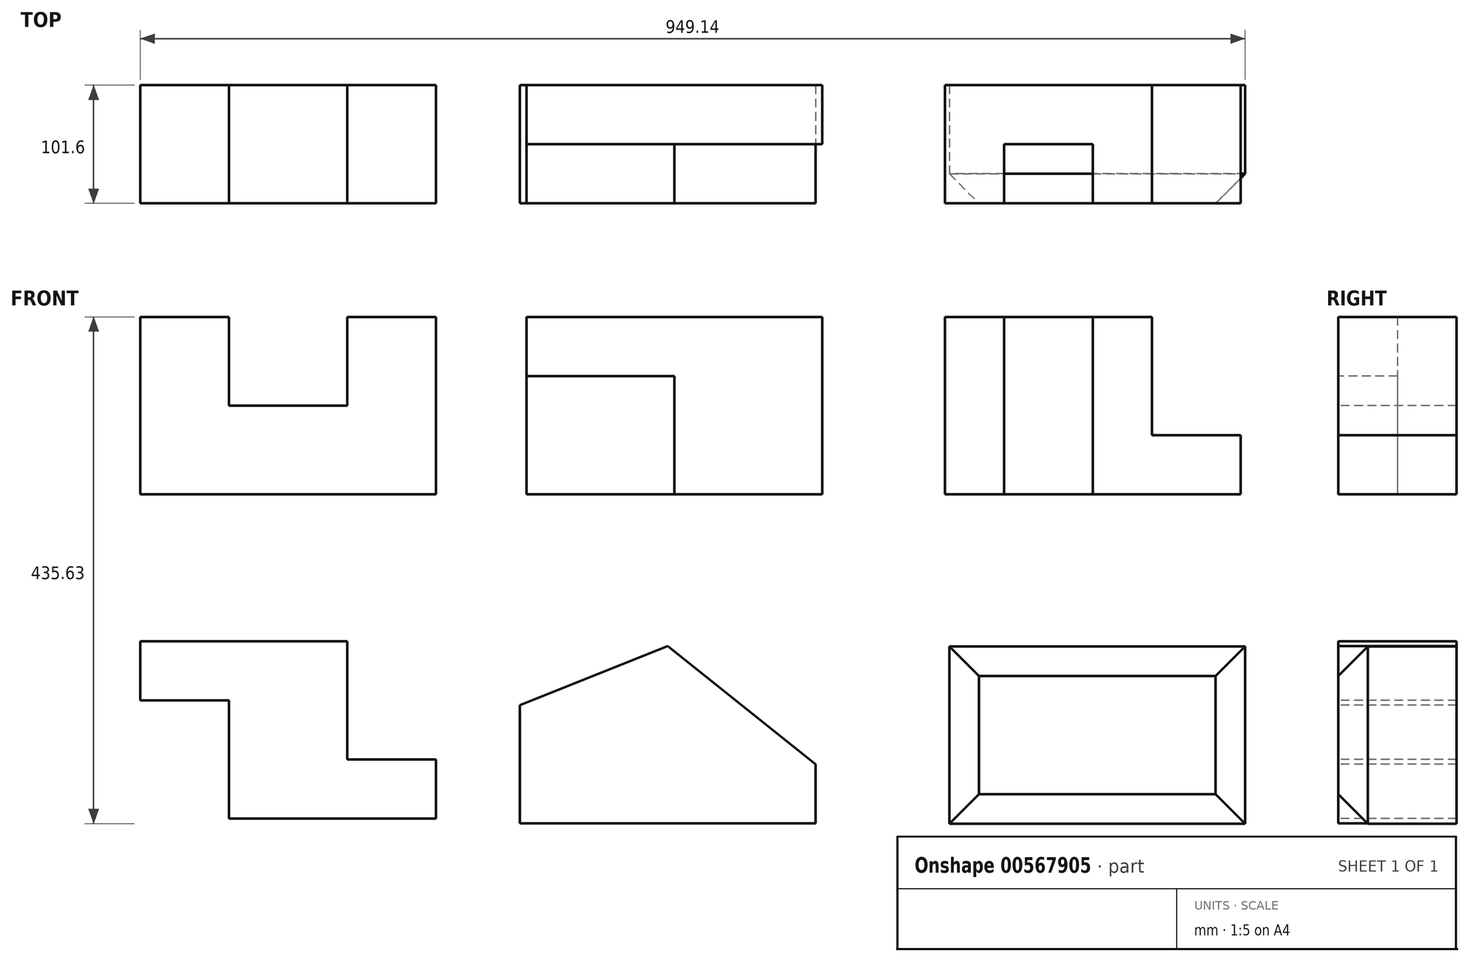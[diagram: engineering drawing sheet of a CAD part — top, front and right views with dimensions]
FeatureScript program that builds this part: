
annotation { "Feature Type Name" : "Feature", "Feature Type Description" : "" }
export const myFeature = defineFeature(function(context is Context, id is Id, definition is map)
    precondition{}
    {
        {
            var Q0;
            Q0=qCreatedBy(makeId("Front.planeOp"),FACE);
            var sketch = newSketch(context, id + "F0", { "sketchPlane" : qUnion([Q0])});
            skLineSegment(sketch, "E0", {"start": v(0, 0) * mm, "end": v(254, 0) * mm});
            skLineSegment(sketch, "E1", {"start": v(0, 152.4) * mm, "end": v(76.2, 152.4) * mm});
            skLineSegment(sketch, "E2", {"start": v(76.2, 152.4) * mm, "end": v(76.2, 76.2) * mm});
            skLineSegment(sketch, "E3", {"start": v(76.2, 76.2) * mm, "end": v(177.8, 76.2) * mm});
            skLineSegment(sketch, "E4", {"start": v(177.8, 76.2) * mm, "end": v(177.8, 152.4) * mm});
            skLineSegment(sketch, "E5", {"start": v(177.8, 152.4) * mm, "end": v(254, 152.4) * mm});
            skLineSegment(sketch, "E6", {"start": v(254, 152.4) * mm, "end": v(254, 0) * mm});
            skLineSegment(sketch, "E7", {"start": v(0, 0) * mm, "end": v(0, 152.4) * mm});
            skSolve(sketch);
        }
        {
            var Q0;
            Q0=makeQuery(id+"F0.imprint","IMPRINT",FACE,{"disambiguationData":[TD([[makeQuery(id+"F0.imprint","IMPRINT",EDGE,{"derivedFrom":sQuery(id+"F0.wireOp",EDGE,"E0")}),1.0]])]});
            extrude(context, id + "F1", {"entities" : qUnion([Q0]), "oppositeDirection" : true, "depth" : 101.6 * mm, "offsetDistance" : 25.4 * mm});
        }
        {
            var Q0;
            Q0=qCreatedBy(makeId("Top.planeOp"),FACE);
            var sketch = newSketch(context, id + "F2", { "sketchPlane" : qUnion([Q0])});
            skLineSegment(sketch, "E8", {"start": v(331.96, 0) * mm, "end": v(331.96, 101.6) * mm});
            skLineSegment(sketch, "E9", {"start": v(331.96, 101.6) * mm, "end": v(585.96, 101.6) * mm});
            skLineSegment(sketch, "E10", {"start": v(585.96, 101.6) * mm, "end": v(585.96, 50.8) * mm});
            skLineSegment(sketch, "E11", {"start": v(585.96, 50.8) * mm, "end": v(458.96, 50.8) * mm});
            skLineSegment(sketch, "E12", {"start": v(458.96, 50.8) * mm, "end": v(458.96, 0) * mm});
            skLineSegment(sketch, "E13", {"start": v(458.96, 0) * mm, "end": v(331.96, 0) * mm});
            skSolve(sketch);
        }
        {
            var Q0;
            Q0=makeQuery(id+"F2.imprint","IMPRINT",FACE,{"disambiguationData":[TD([[makeQuery(id+"F2.imprint","IMPRINT",EDGE,{"derivedFrom":sQuery(id+"F2.wireOp",EDGE,"E8")}),-1.0]])]});
            extrude(context, id + "F3", {"entities" : qUnion([Q0]), "depth" : 152.4 * mm, "offsetDistance" : 25.4 * mm});
        }
        {
            var Q0;
            Q0=qCreatedBy(makeId("Top.planeOp"),FACE);
            var sketch = newSketch(context, id + "F4", { "sketchPlane" : qUnion([Q0])});
            skLineSegment(sketch, "E14", {"start": v(691.2, 0) * mm, "end": v(691.2, 101.6) * mm});
            skLineSegment(sketch, "E15", {"start": v(691.2, 101.6) * mm, "end": v(945.2, 101.6) * mm});
            skLineSegment(sketch, "E16", {"start": v(945.2, 101.6) * mm, "end": v(945.2, 0) * mm});
            skLineSegment(sketch, "E17", {"start": v(691.2, 0) * mm, "end": v(742, 0) * mm});
            skLineSegment(sketch, "E18", {"start": v(742, 0) * mm, "end": v(742, 50.8) * mm});
            skLineSegment(sketch, "E19", {"start": v(742, 50.8) * mm, "end": v(818.2, 50.8) * mm});
            skLineSegment(sketch, "E20", {"start": v(818.2, 50.8) * mm, "end": v(818.2, 0) * mm});
            skLineSegment(sketch, "E21", {"start": v(818.2, 0) * mm, "end": v(945.2, 0) * mm});
            skSolve(sketch);
        }
        {
            var Q0;
            Q0=makeQuery(id+"F4.imprint","IMPRINT",FACE,{"disambiguationData":[TD([[makeQuery(id+"F4.imprint","IMPRINT",EDGE,{"derivedFrom":sQuery(id+"F4.wireOp",EDGE,"E14")}),-1.0]])]});
            extrude(context, id + "F5", {"entities" : qUnion([Q0]), "depth" : 152.4 * mm, "offsetDistance" : 25.4 * mm});
        }
        {
            var Q0;
            Q0=makeQuery(id+"F3.opExtrude","SWEPT_FACE",FACE,{"disambiguationData":[OSD([sQuery(id+"F2.wireOp",EDGE,"E13")])]});
            var sketch = newSketch(context, id + "F6", { "sketchPlane" : qUnion([Q0])});
            skLineSegment(sketch, "E22.bottom", {"start": v(331.96, 152.4) * mm, "end": v(458.96, 152.4) * mm});
            skLineSegment(sketch, "E22.top", {"start": v(331.96, 101.6) * mm, "end": v(458.96, 101.6) * mm});
            skLineSegment(sketch, "E22.left", {"start": v(331.96, 152.4) * mm, "end": v(331.96, 101.6) * mm});
            skLineSegment(sketch, "E22.right", {"start": v(458.96, 152.4) * mm, "end": v(458.96, 101.6) * mm});
            skSolve(sketch);
        }
        {
            var Q0;
            Q0=makeQuery(id+"F6.imprint","IMPRINT",FACE,{"disambiguationData":[TD([[makeQuery(id+"F6.imprint","IMPRINT",EDGE,{"derivedFrom":sQuery(id+"F6.wireOp",EDGE,"E22.bottom")}),1.0]])]});
            extrude(context, id + "F7", {"entities" : qUnion([Q0]), "operationType" : NewBodyOperationType.REMOVE, "oppositeDirection" : true, "depth" : 50.8 * mm, "offsetDistance" : 25.4 * mm});
        }
        {
            var Q0;
            Q0=makeQuery(id+"F5.opExtrude","SWEPT_FACE",FACE,{"disambiguationData":[OSD([sQuery(id+"F4.wireOp",EDGE,"E16")])]});
            var sketch = newSketch(context, id + "F8", { "sketchPlane" : qUnion([Q0])});
            skLineSegment(sketch, "E23.bottom", {"start": v(0, 152.4) * mm, "end": v(101.6, 152.4) * mm});
            skLineSegment(sketch, "E23.top", {"start": v(0, 50.8) * mm, "end": v(101.6, 50.8) * mm});
            skLineSegment(sketch, "E23.left", {"start": v(0, 152.4) * mm, "end": v(0, 50.8) * mm});
            skLineSegment(sketch, "E23.right", {"start": v(101.6, 152.4) * mm, "end": v(101.6, 50.8) * mm});
            skSolve(sketch);
        }
        {
            var Q0;
            Q0 = qSketchRegion(id + "F8", true);
            extrude(context, id + "F9", {"entities" : qUnion([Q0]), "operationType" : NewBodyOperationType.REMOVE, "oppositeDirection" : true, "depth" : 76.2 * mm, "offsetDistance" : 25.4 * mm});
        }
        {
            var Q0;
            Q0=qCreatedBy(makeId("Front.planeOp"),FACE);
            var sketch = newSketch(context, id + "F10", { "sketchPlane" : qUnion([Q0])});
            skLineSegment(sketch, "E24", {"start": v(0, -126.4) * mm, "end": v(254, -126.4) * mm});
            skLineSegment(sketch, "E25", {"start": v(254, -126.4) * mm, "end": v(254, -278.8) * mm});
            skLineSegment(sketch, "E26", {"start": v(254, -278.8) * mm, "end": v(0, -278.8) * mm});
            skLineSegment(sketch, "E27", {"start": v(0, -278.8) * mm, "end": v(0, -126.4) * mm});
            skSolve(sketch);
        }
        {
            var Q0;
            Q0=makeQuery(id+"F10.imprint","IMPRINT",FACE,{"disambiguationData":[TD([[makeQuery(id+"F10.imprint","IMPRINT",EDGE,{"derivedFrom":sQuery(id+"F10.wireOp",EDGE,"E24")}),-1.0]])]});
            extrude(context, id + "F11", {"entities" : qUnion([Q0]), "oppositeDirection" : true, "depth" : 101.6 * mm, "offsetDistance" : 25.4 * mm});
        }
        {
            var Q0;
            Q0=makeQuery(id+"F11.opExtrude","CAP_FACE",FACE,{"disambiguationData":[OSD([sQuery(id+"F10.wireOp",EDGE,"E24"),sQuery(id+"F10.wireOp",EDGE,"E25"),sQuery(id+"F10.wireOp",EDGE,"E26"),sQuery(id+"F10.wireOp",EDGE,"E27")])],"isStart":true});
            var sketch = newSketch(context, id + "F12", { "sketchPlane" : qUnion([Q0])});
            skLineSegment(sketch, "E28.bottom", {"start": v(0, -278.8) * mm, "end": v(76.2, -278.8) * mm});
            skLineSegment(sketch, "E28.top", {"start": v(0, -177.2) * mm, "end": v(76.2, -177.2) * mm});
            skLineSegment(sketch, "E28.left", {"start": v(0, -278.8) * mm, "end": v(0, -177.2) * mm});
            skLineSegment(sketch, "E28.right", {"start": v(76.2, -278.8) * mm, "end": v(76.2, -177.2) * mm});
            skLineSegment(sketch, "E29.bottom", {"start": v(254, -126.4) * mm, "end": v(177.8, -126.4) * mm});
            skLineSegment(sketch, "E29.top", {"start": v(254, -228) * mm, "end": v(177.8, -228) * mm});
            skLineSegment(sketch, "E29.left", {"start": v(254, -126.4) * mm, "end": v(254, -228) * mm});
            skLineSegment(sketch, "E29.right", {"start": v(177.8, -126.4) * mm, "end": v(177.8, -228) * mm});
            skSolve(sketch);
        }
        {
            var Q0;
            Q0=makeQuery(id+"F12.imprint","IMPRINT",FACE,{"disambiguationData":[TD([[makeQuery(id+"F12.imprint","IMPRINT",EDGE,{"derivedFrom":sQuery(id+"F12.wireOp",EDGE,"E28.bottom")}),-1.0]])]});
            var Q1;
            Q1=makeQuery(id+"F12.imprint","IMPRINT",FACE,{"disambiguationData":[TD([[makeQuery(id+"F12.imprint","IMPRINT",EDGE,{"derivedFrom":sQuery(id+"F12.wireOp",EDGE,"E29.bottom")}),-1.0]])]});
            extrude(context, id + "F13", {"entities" : qUnion([Q0, Q1]), "operationType" : NewBodyOperationType.REMOVE, "oppositeDirection" : true, "depth" : 101.6 * mm, "offsetDistance" : 25.4 * mm});
        }
        {
            var Q0;
            Q0=qCreatedBy(makeId("Front.planeOp"),FACE);
            var sketch = newSketch(context, id + "F14", { "sketchPlane" : qUnion([Q0])});
            skLineSegment(sketch, "E30", {"start": v(326.29, -130.56) * mm, "end": v(326.29, -282.96) * mm});
            skLineSegment(sketch, "E31", {"start": v(326.29, -130.56) * mm, "end": v(580.29, -130.56) * mm});
            skLineSegment(sketch, "E32", {"start": v(580.29, -130.56) * mm, "end": v(580.29, -282.96) * mm});
            skLineSegment(sketch, "E33", {"start": v(580.29, -282.96) * mm, "end": v(326.29, -282.96) * mm});
            skSolve(sketch);
        }
        {
            var Q0;
            Q0 = qSketchRegion(id + "F14", true);
            extrude(context, id + "F15", {"entities" : qUnion([Q0]), "oppositeDirection" : true, "depth" : 101.6 * mm, "offsetDistance" : 25.4 * mm});
        }
        {
            var Q0;
            Q0=makeQuery(id+"F15.opExtrude","CAP_FACE",FACE,{"disambiguationData":[OSD([sQuery(id+"F14.wireOp",EDGE,"E30"),sQuery(id+"F14.wireOp",EDGE,"E31"),sQuery(id+"F14.wireOp",EDGE,"E32"),sQuery(id+"F14.wireOp",EDGE,"E33")])],"isStart":true});
            var sketch = newSketch(context, id + "F16", { "sketchPlane" : qUnion([Q0])});
            skLineSegment(sketch, "E34", {"start": v(326.29, -282.96) * mm, "end": v(326.29, -181.36) * mm});
            skLineSegment(sketch, "E35", {"start": v(453.29, -282.96) * mm, "end": v(453.29, -130.56) * mm});
            skLineSegment(sketch, "E36", {"start": v(326.29, -181.36) * mm, "end": v(453.29, -130.56) * mm});
            skSolve(sketch);
        }
        {
            var Q0;
            {var subQ0=sQuery(id+"F16.wireOp",EDGE,"E36");Q0=makeQuery(id+"F16.imprint","IMPRINT",FACE,{"disambiguationData":[TD([[makeQuery(id+"F16.imprint","IMPRINT",EDGE,{"derivedFrom":subQ0}),1.0]])]});}
            extrude(context, id + "F17", {"entities" : qUnion([Q0]), "operationType" : NewBodyOperationType.REMOVE, "oppositeDirection" : true, "depth" : 101.6 * mm, "offsetDistance" : 25.4 * mm});
        }
        {
            var Q0;
            Q0=makeQuery(id+"F15.opExtrude","CAP_FACE",FACE,{"disambiguationData":[OSD([sQuery(id+"F14.wireOp",EDGE,"E30"),sQuery(id+"F14.wireOp",EDGE,"E31"),sQuery(id+"F14.wireOp",EDGE,"E32"),sQuery(id+"F14.wireOp",EDGE,"E33")])],"isStart":true});
            var sketch = newSketch(context, id + "F18", { "sketchPlane" : qUnion([Q0])});
            skLineSegment(sketch, "E37", {"start": v(580.29, -282.96) * mm, "end": v(580.29, -232.16) * mm});
            skLineSegment(sketch, "E38", {"start": v(453.29, -282.96) * mm, "end": v(453.29, -130.56) * mm});
            skLineSegment(sketch, "E39", {"start": v(453.29, -130.56) * mm, "end": v(580.29, -232.16) * mm});
            skSolve(sketch);
        }
        {
            var Q0;
            {var subQ0=sQuery(id+"F18.wireOp",EDGE,"E39");Q0=makeQuery(id+"F18.imprint","IMPRINT",FACE,{"disambiguationData":[TD([[makeQuery(id+"F18.imprint","IMPRINT",EDGE,{"derivedFrom":subQ0}),1.0]])]});}
            extrude(context, id + "F19", {"entities" : qUnion([Q0]), "operationType" : NewBodyOperationType.REMOVE, "oppositeDirection" : true, "depth" : 101.6 * mm, "offsetDistance" : 25.4 * mm});
        }
        {
            var Q0;
            Q0=qCreatedBy(makeId("Front.planeOp"),FACE);
            var sketch = newSketch(context, id + "F20", { "sketchPlane" : qUnion([Q0])});
            skLineSegment(sketch, "E40", {"start": v(695.14, -130.83) * mm, "end": v(949.14, -130.83) * mm});
            skLineSegment(sketch, "E41", {"start": v(949.14, -130.83) * mm, "end": v(949.14, -283.23) * mm});
            skLineSegment(sketch, "E42", {"start": v(949.14, -283.23) * mm, "end": v(695.14, -283.23) * mm});
            skLineSegment(sketch, "E43", {"start": v(695.14, -283.23) * mm, "end": v(695.14, -130.83) * mm});
            skSolve(sketch);
        }
        {
            var Q0;
            Q0=makeQuery(id+"F20.imprint","IMPRINT",FACE,{"disambiguationData":[TD([[makeQuery(id+"F20.imprint","IMPRINT",EDGE,{"derivedFrom":sQuery(id+"F20.wireOp",EDGE,"E40")}),-1.0]])]});
            extrude(context, id + "F21", {"entities" : qUnion([Q0]), "oppositeDirection" : true, "depth" : 101.6 * mm, "offsetDistance" : 25.4 * mm});
        }
        {
            var Q0;
            Q0=makeQuery(id+"F21.opExtrude","CAP_EDGE",EDGE,{"disambiguationData":[OSD([sQuery(id+"F20.wireOp",EDGE,"E40")])],"isStart":true});
            chamfer(context, id + "F22", {"entities" : qUnion([Q0]), "width" : 25.4 * mm, "tangentPropagation" : true});
        }
        {
            var Q0;
            Q0=makeQuery(id+"F21.opExtrude","CAP_EDGE",EDGE,{"disambiguationData":[OSD([sQuery(id+"F20.wireOp",EDGE,"E43")])],"isStart":true});
            chamfer(context, id + "F23", {"entities" : qUnion([Q0]), "width" : 25.4 * mm, "tangentPropagation" : true});
        }
        {
            var Q0;
            Q0=makeQuery(id+"F21.opExtrude","CAP_EDGE",EDGE,{"disambiguationData":[OSD([sQuery(id+"F20.wireOp",EDGE,"E42")])],"isStart":true});
            chamfer(context, id + "F24", {"entities" : qUnion([Q0]), "width" : 25.4 * mm, "tangentPropagation" : true});
        }
        {
            var Q0;
            Q0=makeQuery(id+"F21.opExtrude","CAP_EDGE",EDGE,{"disambiguationData":[OSD([sQuery(id+"F20.wireOp",EDGE,"E41")])],"isStart":true});
            chamfer(context, id + "F25", {"entities" : qUnion([Q0]), "width" : 25.4 * mm, "tangentPropagation" : true});
        }
    });
